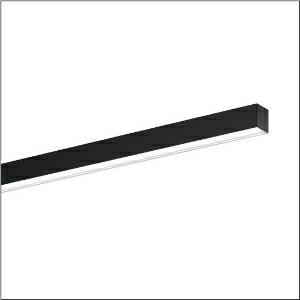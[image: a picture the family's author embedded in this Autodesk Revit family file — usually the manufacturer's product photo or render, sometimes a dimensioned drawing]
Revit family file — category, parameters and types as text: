
# Revit family: silica_r__21_51mx20tat2b_5805
name_source: partatom
category: Lighting Fixtures
units: mm (PartAtom-declared; Revit-internal decimal feet)

## family parameters
Cut with Voids When Loaded = No
Host = Face
Light Source = No
Part Type = Normal
Room Calculation Point = No
Round Connector Dimension = Use Diameter
Shared = No

## types (1)
- --- (1 x LED, 2400 lm, 20.5 W, 6500K)
    Apparent Load = 21 VA
    CIE Flux Codes = 48 79 96 100 100
    Color Rendering = 80
    Color Temperature = 6500K
    Default Elevation = 1800 mm
    Description = Silica® 21, office luminaire, primary optical cover: cover, of PMMA, opal, light emission: direct distribution, primary light characteristic: symmetric, installation type: surface-mounted, LED, rated luminous flux: 2.400lm, luminous efficacy: 112lm/W, light colour: 8tw, colour temperature: 2700..6500K, control gear: DALI DT8, with terminal, 3+2-pole, max. 2.5mm², mains connection: 220..240V, AC, 50/60Hz, rated input power: 21.5W, luminaire housing, of aluminium, matt jet black (RAL 9005), length: 1.204mm, width: 53mm, height: 53mm, protection rating (complete): IP20, insulation class (complete): insulation class I (protective earthing), certification: CE, permissible operating ambient temperature: 0..+35°C, standard: EN 50419, packaging unit: 1 piece
    Height = 53 mm
    Lamp = 1 x LED
    Lamp Light Flux = 2400 lm
    Lamp Power = 20.5 W
    Lamp count = 1
    Length = 1204 mm
    Luminous efficacy = 117 lm/W
    Manufacturer = Siteco
    ModVariant = No
    Model = 51MX20TAT2B
    Mounting Place = Ceiling
    Mounting Type = Surface mounted
    Number of Poles = 1
    OnlyDefault = Yes
    Power Factor = 1
    Product Name = Silica® 21
    Product group = office luminaire | ceiling mounted
    ProductGroupID = 302
    Protection Class = Protection class I
    Protection Degree = IP 20
    RLX_Detail_Level = 1
    RLX_Emergency_Light_Flux = 0 lm
    RLX_Emergency_Type = 0
    RLX_Emergency_Type_DB = No
    RlxData = <blob elided: 25641 chars, md5=4f69e36c>
    Socket = socket
    Standby Power = 0 W
    System Light Flux = 2400 lm
    System Power = 21 W
    Type Comments = individual setting
    Type Image = l_1335925.jpg
    URL = http://relux.com
    VarID = @adj_139692
    Voltage = 0 V
    Weight = 0.00 kg
    Width = 53 mm

## geometry (parser evidence)
native form markers: Blend x4, Sweep x10
no freeform markers — native parametric forms only
